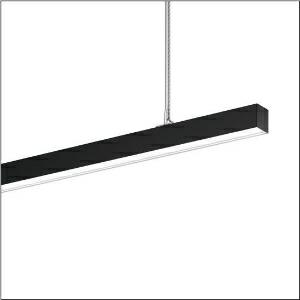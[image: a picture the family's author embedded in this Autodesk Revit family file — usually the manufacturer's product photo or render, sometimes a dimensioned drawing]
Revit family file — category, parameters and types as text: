
# Revit family: silica_r__21_51mx30da44bb_2b52
name_source: partatom
category: Lighting Fixtures
units: mm (PartAtom-declared; Revit-internal decimal feet)

## family parameters
Cut with Voids When Loaded = No
Host = Face
Light Source = No
Part Type = Normal
Room Calculation Point = No
Round Connector Dimension = Use Diameter
Shared = No

## types (1)
- --- (1 x LED, 4210 lm, 26 W, 4000K)
    Apparent Load = 26 VA
    CIE Flux Codes = 47 79 96 57 100
    Color Rendering = 80
    Color Temperature = 4000K
    Default Elevation = 1800 mm
    Description = Silica® 21, office luminaire, primary optical cover: cover, of PMMA, opal, light emission: direct/indirect distribution, primary light characteristic: symmetric, installation type: suspended mounting, LED, rated luminous flux: 4.210lm, luminous efficacy: 162lm/W, light colour: 840, colour temperature: 4000K, control gear: DALI 2, with terminal, 3+2-pole, max. 2.5mm², mains connection: 220..240V, AC, 50/60Hz, rated input power: 26W, luminaire housing, of aluminium, matt jet black (RAL 9005), length: 1.204mm, width: 53mm, height: 53mm, protection rating (complete): IP20, insulation class (complete): insulation class I (protective earthing), certification: CE, permissible operating ambient temperature: 0..+35°C, standard: EN 50419, packaging unit: 1 piece
    Height = 53 mm
    Lamp = 1 x LED
    Lamp Light Flux = 4210 lm
    Lamp Power = 26 W
    Lamp count = 1
    Length = 1204 mm
    Luminous efficacy = 162 lm/W
    Manufacturer = Siteco
    ModVariant = No
    Model = 51MX30DA44BB
    Mounting Place = Ceiling
    Mounting Type = Pendant
    Number of Poles = 1
    OnlyDefault = Yes
    Power Factor = 1
    Product Name = Silica® 21
    Product group = office luminaire | ceiling pendant
    ProductGroupID = 904
    Protection Class = Protection class I
    Protection Degree = IP 20
    RLX_Detail_Level = 1
    RLX_Emergency_Light_Flux = 0 lm
    RLX_Emergency_Type = 0
    RLX_Emergency_Type_DB = No
    RlxData = <blob elided: 25829 chars, md5=86e442c8>
    Socket = socket
    Standby Power = 0 W
    System Light Flux = 4210 lm
    System Power = 26 W
    Type Comments = factory setting: luminous flux: 100 % | dim-lin: 254 | 218 mA
    Type Image = l_1335856.jpg
    URL = http://relux.com
    VarID = @adj_117350
    Voltage = 0 V
    Weight = 0.00 kg
    Width = 53 mm

## geometry (parser evidence)
native form markers: Blend x4, Sweep x13
no freeform markers — native parametric forms only
